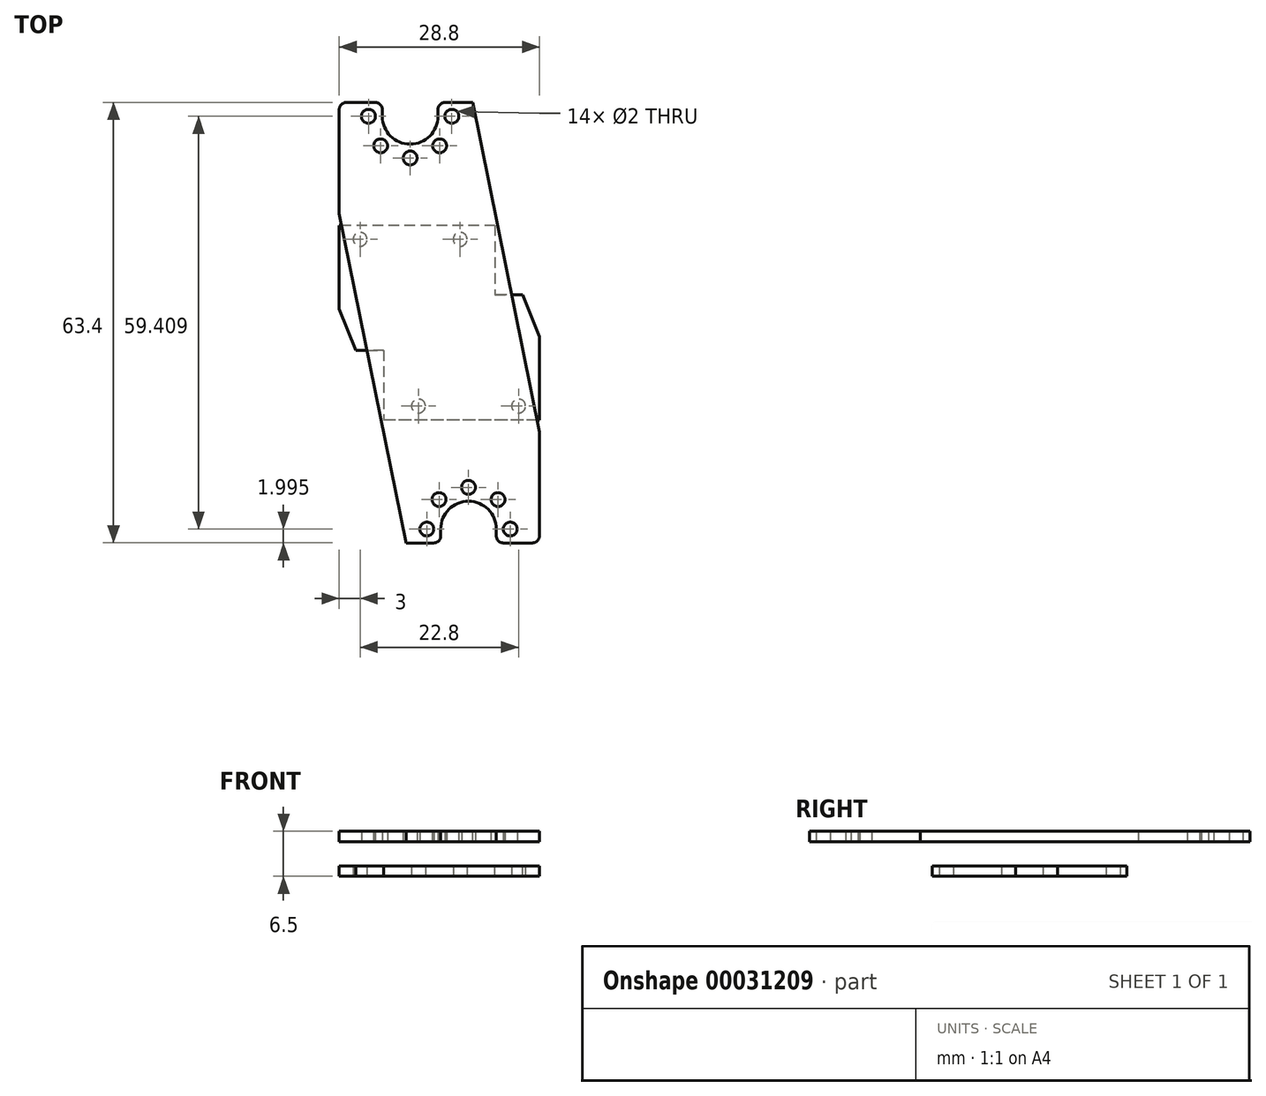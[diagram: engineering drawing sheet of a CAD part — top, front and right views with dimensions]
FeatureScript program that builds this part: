
annotation { "Feature Type Name" : "Feature", "Feature Type Description" : "" }
export const myFeature = defineFeature(function(context is Context, id is Id, definition is map)
    precondition{}
    {
        {
            var Q0;
            Q0=qCreatedBy(makeId("Top.planeOp"),FACE);
            var sketch = newSketch(context, id + "F0", { "sketchPlane" : qUnion([Q0])});
            skLineSegment(sketch, "E0.bottom", {"start": v(14.4, -14) * mm, "end": v(-14.4, -14) * mm});
            skLineSegment(sketch, "E0.top", {"start": v(14.4, 14) * mm, "end": v(-14.4, 14) * mm});
            skLineSegment(sketch, "E0.left", {"start": v(14.4, -14) * mm, "end": v(14.4, 14) * mm});
            skLineSegment(sketch, "E0.right", {"start": v(-14.4, -14) * mm, "end": v(-14.4, 14) * mm});
            skPoint(sketch, "E0.middle", {"position": v(0, 0) * mm});
            skCircle(sketch, "E1", {"center": v(-11.4, 12) * mm, "radius": 1 * mm});
            skCircle(sketch, "E2", {"center": v(3, 12) * mm, "radius": 1 * mm});
            skCircle(sketch, "E3", {"center": v(-4.2, 29.7) * mm, "radius": 6 * mm, "construction": true});
            skLineSegment(sketch, "E4", {"start": v(-11.4, 12) * mm, "end": v(3, 12) * mm, "construction": true});
            skPoint(sketch, "E5", {"position": v(-4.2, 12) * mm});
            skCircle(sketch, "E6.MirrorC", {"center": v(11.4, 12) * mm, "radius": 1 * mm, "construction": true});
            skCircle(sketch, "E7.MirrorC", {"center": v(-3, 12) * mm, "radius": 1 * mm, "construction": true});
            skCircle(sketch, "E8.MirrorC", {"center": v(-3, -12) * mm, "radius": 1 * mm});
            skCircle(sketch, "E9.MirrorC", {"center": v(11.4, -12) * mm, "radius": 1 * mm});
            skSolve(sketch);
        }
        {
            var Q0;
            Q0=qSketchRegion(id+"F0",true);
            extrude(context, id + "F1", {"entities" : qUnion([Q0]), "depth" : 1.5 * mm});
        }
        {
            var Q0;
            Q0=makeQuery(id+"F1.opExtrude","CAP_FACE",FACE,{"disambiguationData":[OSD([sQuery(id+"F0.wireOp",EDGE,"E0.bottom"),sQuery(id+"F0.wireOp",EDGE,"E0.top"),sQuery(id+"F0.wireOp",EDGE,"E0.left"),sQuery(id+"F0.wireOp",EDGE,"E0.right"),sQuery(id+"F0.wireOp",EDGE,"E1"),sQuery(id+"F0.wireOp",EDGE,"E2"),sQuery(id+"F0.wireOp",EDGE,"E8.MirrorC"),sQuery(id+"F0.wireOp",EDGE,"E9.MirrorC")])],"isStart":false});
            var sketch = newSketch(context, id + "F2", { "sketchPlane" : qUnion([Q0])});
            skPoint(sketch, "E10", {"position": v(-11.4, 12) * mm});
            skPoint(sketch, "E11", {"position": v(3, 12) * mm});
            skPoint(sketch, "E12", {"position": v(-3, -12) * mm});
            skPoint(sketch, "E13", {"position": v(11.4, -12) * mm});
            skLineSegment(sketch, "E14", {"start": v(-14.4, 2) * mm, "end": v(-12, -4) * mm});
            skLineSegment(sketch, "E15", {"start": v(-8, -14) * mm, "end": v(-14.4, -14) * mm});
            skLineSegment(sketch, "E16", {"start": v(-14.4, -14) * mm, "end": v(-14.4, 2) * mm});
            skLineSegment(sketch, "E17.MirrorCS", {"start": v(14.4, 2) * mm, "end": v(8, -14) * mm, "construction": true});
            skLineSegment(sketch, "E18.MirrorCS", {"start": v(14.4, -14) * mm, "end": v(14.4, 2) * mm, "construction": true});
            skLineSegment(sketch, "E19.MirrorCS", {"start": v(8, -14) * mm, "end": v(14.4, -14) * mm, "construction": true});
            skLineSegment(sketch, "E20.MirrorCS", {"start": v(12, 4) * mm, "end": v(10.4, 8) * mm});
            skLineSegment(sketch, "E21.MirrorCS", {"start": v(14.4, 14) * mm, "end": v(14.4, -2) * mm});
            skLineSegment(sketch, "E22.MirrorCS", {"start": v(8, 14) * mm, "end": v(14.4, 14) * mm});
            skLineSegment(sketch, "E23", {"start": v(8, 14) * mm, "end": v(8, 4) * mm});
            skLineSegment(sketch, "E24", {"start": v(8, 4) * mm, "end": v(12, 4) * mm});
            skLineSegment(sketch, "E25", {"start": v(10.4, 8) * mm, "end": v(10.4, -2) * mm, "construction": true});
            skLineSegment(sketch, "E26", {"start": v(10.4, -2) * mm, "end": v(14.4, -2) * mm, "construction": true});
            skLineSegment(sketch, "E27", {"start": v(10.4, 8) * mm, "end": v(14.4, -2) * mm});
            skLineSegment(sketch, "E28", {"start": v(-12, -4) * mm, "end": v(-8, -4) * mm});
            skLineSegment(sketch, "E29", {"start": v(-8, -4) * mm, "end": v(-8, -14) * mm});
            skSolve(sketch);
        }
        {
            var Q0;
            Q0=qSketchRegion(id+"F2",true);
            extrude(context, id + "F3", {"entities" : qUnion([Q0]), "operationType" : NewBodyOperationType.REMOVE, "endBound" : BoundingType.UP_TO_NEXT, "oppositeDirection" : true, "depth" : 25 * mm});
        }
        {
            var Q0;
            Q0=qCreatedBy(makeId("Top.planeOp"),FACE);
            cPlane(context, id + "F4", {"entities" : qUnion([Q0]), "cplaneType" : CPlaneType.OFFSET, "offset" : 5 * mm, "width" : 150 * mm, "height" : 150 * mm});
        }
        {
            var Q0;
            Q0=qCreatedBy(id+"F4.planeOp",FACE);
            var sketch = newSketch(context, id + "F5", { "sketchPlane" : qUnion([Q0])});
            skLineSegment(sketch, "E30.bottom", {"start": v(-14.4, 31.7) * mm, "end": v(-8.2, 31.7) * mm});
            skLineSegment(sketch, "E30.top", {"start": v(-14.4, -31.7) * mm, "end": v(0.2, -31.7) * mm});
            skLineSegment(sketch, "E30.left", {"start": v(-14.4, 31.7) * mm, "end": v(-14.4, -31.7) * mm});
            skLineSegment(sketch, "E30.right", {"start": v(14.4, 31.7) * mm, "end": v(14.4, -31.7) * mm});
            skPoint(sketch, "E30.middle", {"position": v(0, 0) * mm});
            skLineSegment(sketch, "E31.0", {"start": v(-14.4, -14) * mm, "end": v(-14.4, 14) * mm, "construction": true});
            skLineSegment(sketch, "E32.0", {"start": v(14.4, -14) * mm, "end": v(14.4, 14) * mm, "construction": true});
            skCircle(sketch, "E33.0", {"center": v(-4.2, 29.7) * mm, "radius": 6 * mm, "construction": true});
            skArc(sketch, "E34", {"start": v(-8.2, 29.7) * mm, "mid": v(-4.2, 25.7) * mm, "end": v(-0.2, 29.7) * mm});
            skCircle(sketch, "E35", {"center": v(-4.2, 23.7) * mm, "radius": 1 * mm});
            skCircle(sketch, "E36.1.0", {"center": v(0.04, 25.46) * mm, "radius": 1 * mm});
            skCircle(sketch, "E36.2.0", {"center": v(1.8, 29.7) * mm, "radius": 1 * mm});
            skCircle(sketch, "E36.6.0", {"center": v(-10.2, 29.7) * mm, "radius": 1 * mm});
            skCircle(sketch, "E36.7.0", {"center": v(-8.44, 25.46) * mm, "radius": 1 * mm});
            skLineSegment(sketch, "E37", {"start": v(-8.2, 29.7) * mm, "end": v(-8.2, 31.7) * mm});
            skLineSegment(sketch, "E38", {"start": v(-0.2, 29.7) * mm, "end": v(-0.2, 31.7) * mm});
            skLineSegment(sketch, "E39.trimOffspring", {"start": v(-0.2, 31.7) * mm, "end": v(14.4, 31.7) * mm});
            skLineSegment(sketch, "E40.MirrorCS", {"start": v(8.2, 29.7) * mm, "end": v(8.2, 31.7) * mm, "construction": true});
            skLineSegment(sketch, "E41.MirrorCS", {"start": v(0.2, 29.7) * mm, "end": v(0.2, 31.7) * mm, "construction": true});
            skArc(sketch, "E42.MirrorCS", {"start": v(8.2, 29.7) * mm, "mid": v(4.2, 25.7) * mm, "end": v(0.2, 29.7) * mm, "construction": true});
            skCircle(sketch, "E43.MirrorC", {"center": v(-1.8, 29.7) * mm, "radius": 1 * mm, "construction": true});
            skCircle(sketch, "E44.MirrorC", {"center": v(-0.04, 25.46) * mm, "radius": 1 * mm, "construction": true});
            skCircle(sketch, "E45.MirrorC", {"center": v(4.2, 23.7) * mm, "radius": 1 * mm, "construction": true});
            skCircle(sketch, "E46.MirrorC", {"center": v(8.44, 25.46) * mm, "radius": 1 * mm, "construction": true});
            skCircle(sketch, "E47.MirrorC", {"center": v(10.2, 29.7) * mm, "radius": 1 * mm, "construction": true});
            skLineSegment(sketch, "E48.MirrorCS", {"start": v(0.2, -29.7) * mm, "end": v(0.2, -31.7) * mm});
            skLineSegment(sketch, "E49.MirrorCS", {"start": v(8.2, -29.7) * mm, "end": v(8.2, -31.7) * mm});
            skArc(sketch, "E50.MirrorCS", {"start": v(8.2, -29.7) * mm, "mid": v(4.2, -25.7) * mm, "end": v(0.2, -29.7) * mm});
            skCircle(sketch, "E51.MirrorC", {"center": v(-0.04, -25.46) * mm, "radius": 1 * mm});
            skCircle(sketch, "E52.MirrorC", {"center": v(8.44, -25.46) * mm, "radius": 1 * mm});
            skCircle(sketch, "E53.MirrorC", {"center": v(10.2, -29.7) * mm, "radius": 1 * mm});
            skCircle(sketch, "E54.MirrorC", {"center": v(4.2, -23.7) * mm, "radius": 1 * mm});
            skCircle(sketch, "E55.MirrorC", {"center": v(-1.8, -29.7) * mm, "radius": 1 * mm});
            skLineSegment(sketch, "E56.trimOffspring", {"start": v(8.2, -31.7) * mm, "end": v(14.4, -31.7) * mm});
            skSolve(sketch);
        }
        {
            var Q0;
            Q0 = qSketchRegion(id + "F5", true);
            extrude(context, id + "F6", {"entities" : qUnion([Q0]), "depth" : 1.5 * mm});
        }
        {
            var Q0;
            Q0=makeQuery(id+"F6.opExtrude","CAP_FACE",FACE,{"disambiguationData":[OSD([sQuery(id+"F5.wireOp",EDGE,"E30.bottom"),sQuery(id+"F5.wireOp",EDGE,"E30.top"),sQuery(id+"F5.wireOp",EDGE,"E30.left"),sQuery(id+"F5.wireOp",EDGE,"E30.right"),sQuery(id+"F5.wireOp",EDGE,"E34"),sQuery(id+"F5.wireOp",EDGE,"E35"),sQuery(id+"F5.wireOp",EDGE,"E36.1.0"),sQuery(id+"F5.wireOp",EDGE,"E36.2.0"),sQuery(id+"F5.wireOp",EDGE,"E36.6.0"),sQuery(id+"F5.wireOp",EDGE,"E36.7.0"),sQuery(id+"F5.wireOp",EDGE,"E37"),sQuery(id+"F5.wireOp",EDGE,"E38"),sQuery(id+"F5.wireOp",EDGE,"E39.trimOffspring"),sQuery(id+"F5.wireOp",EDGE,"E48.MirrorCS"),sQuery(id+"F5.wireOp",EDGE,"E49.MirrorCS"),sQuery(id+"F5.wireOp",EDGE,"E50.MirrorCS"),sQuery(id+"F5.wireOp",EDGE,"E51.MirrorC"),sQuery(id+"F5.wireOp",EDGE,"E52.MirrorC"),sQuery(id+"F5.wireOp",EDGE,"E53.MirrorC"),sQuery(id+"F5.wireOp",EDGE,"E54.MirrorC"),sQuery(id+"F5.wireOp",EDGE,"E55.MirrorC"),sQuery(id+"F5.wireOp",EDGE,"E56.trimOffspring")])],"isStart":false});
            var sketch = newSketch(context, id + "F7", { "sketchPlane" : qUnion([Q0])});
            skPoint(sketch, "E57", {"position": v(-4.2, 23.7) * mm});
            skPoint(sketch, "E58", {"position": v(-1.8, -29.7) * mm});
            skPoint(sketch, "E59", {"position": v(4.2, -23.7) * mm});
            skPoint(sketch, "E60", {"position": v(1.8, 29.7) * mm});
            skLineSegment(sketch, "E61", {"start": v(-14.4, 15.7) * mm, "end": v(-4.8, -31.7) * mm});
            skLineSegment(sketch, "E62", {"start": v(-4.8, -31.7) * mm, "end": v(-14.4, -31.7) * mm});
            skLineSegment(sketch, "E63", {"start": v(-14.4, -31.7) * mm, "end": v(-14.4, 15.7) * mm});
            skLineSegment(sketch, "E64.MirrorCS", {"start": v(14.4, -31.7) * mm, "end": v(14.4, 15.7) * mm, "construction": true});
            skLineSegment(sketch, "E65.MirrorCS", {"start": v(14.4, 15.7) * mm, "end": v(4.8, -31.7) * mm, "construction": true});
            skLineSegment(sketch, "E66.MirrorCS", {"start": v(4.8, -31.7) * mm, "end": v(14.4, -31.7) * mm, "construction": true});
            skLineSegment(sketch, "E67.MirrorCS", {"start": v(14.4, -15.7) * mm, "end": v(4.8, 31.7) * mm});
            skLineSegment(sketch, "E68.MirrorCS", {"start": v(14.4, 31.7) * mm, "end": v(14.4, -15.7) * mm});
            skLineSegment(sketch, "E69.MirrorCS", {"start": v(4.8, 31.7) * mm, "end": v(14.4, 31.7) * mm});
            skSolve(sketch);
        }
        {
            var Q0;
            Q0 = qSketchRegion(id + "F7", true);
            extrude(context, id + "F8", {"entities" : qUnion([Q0]), "operationType" : NewBodyOperationType.REMOVE, "endBound" : BoundingType.UP_TO_NEXT, "oppositeDirection" : true, "depth" : 25 * mm});
        }
        {
            var Q0;
            Q0=makeQuery(id+"F8.boolean.opBoolean","COPY",EDGE,{"derivedFrom":makeQuery(id+"F8.opExtrude","SWEPT_EDGE",EDGE,{"disambiguationData":[OSD([sQuery(id+"F5.wireOp",EDGE,"E30.top"),sQuery(id+"F7.wireOp",EDGE,"E61"),sQuery(id+"F7.wireOp",EDGE,"E62")])]})});
            var Q1;
            Q1=makeQuery(id+"F6.opExtrude","SWEPT_EDGE",EDGE,{"disambiguationData":[OSD([sQuery(id+"F5.wireOp",EDGE,"E30.top"),sQuery(id+"F5.wireOp",EDGE,"E48.MirrorCS")])]});
            var Q2;
            Q2=makeQuery(id+"F6.opExtrude","SWEPT_EDGE",EDGE,{"disambiguationData":[OSD([sQuery(id+"F5.wireOp",EDGE,"E49.MirrorCS"),sQuery(id+"F5.wireOp",EDGE,"E56.trimOffspring")])]});
            var Q3;
            Q3=makeQuery(id+"F6.opExtrude","SWEPT_EDGE",EDGE,{"disambiguationData":[OSD([sQuery(id+"F5.wireOp",EDGE,"E30.right"),sQuery(id+"F5.wireOp",EDGE,"E56.trimOffspring")])]});
            var Q4;
            Q4=makeQuery(id+"F8.boolean.opBoolean","COPY",EDGE,{"derivedFrom":makeQuery(id+"F8.opExtrude","SWEPT_EDGE",EDGE,{"disambiguationData":[OSD([sQuery(id+"F5.wireOp",EDGE,"E39.trimOffspring"),sQuery(id+"F7.wireOp",EDGE,"E67.MirrorCS"),sQuery(id+"F7.wireOp",EDGE,"E69.MirrorCS")])]})});
            var Q5;
            Q5=makeQuery(id+"F6.opExtrude","SWEPT_EDGE",EDGE,{"disambiguationData":[OSD([sQuery(id+"F5.wireOp",EDGE,"E38"),sQuery(id+"F5.wireOp",EDGE,"E39.trimOffspring")])]});
            var Q6;
            Q6=makeQuery(id+"F6.opExtrude","SWEPT_EDGE",EDGE,{"disambiguationData":[OSD([sQuery(id+"F5.wireOp",EDGE,"E30.bottom"),sQuery(id+"F5.wireOp",EDGE,"E37")])]});
            var Q7;
            Q7=makeQuery(id+"F6.opExtrude","SWEPT_EDGE",EDGE,{"disambiguationData":[OSD([sQuery(id+"F5.wireOp",EDGE,"E30.bottom"),sQuery(id+"F5.wireOp",EDGE,"E30.left")])]});
            fillet(context, id + "F9", {"entities" : qUnion([Q0, Q1, Q2, Q3, Q4, Q5, Q6, Q7]), "radius" : 1 * mm, "tangentPropagation" : true, "allowEdgeOverflow" : false});
        }
    });
